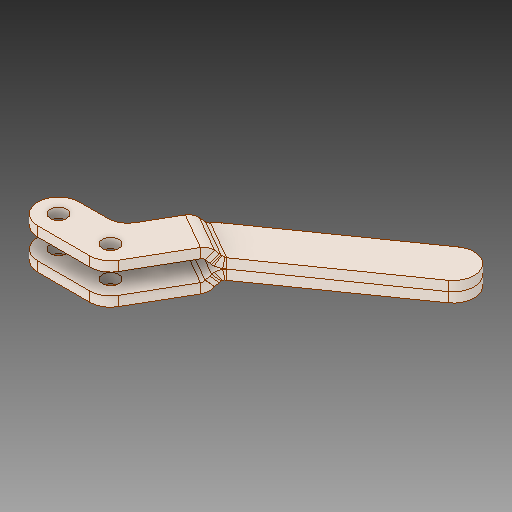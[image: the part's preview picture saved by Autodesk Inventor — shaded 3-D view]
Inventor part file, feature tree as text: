
AUTODESK INVENTOR PART (.ipt)
format: ipt  version: 2019 (Build 230136000, 136)  size: 156,672 bytes
history: mixed  units: in
note: dims shown in document units (in); Inventor stores cm internally (conversion verified against a paired STEP export)
features: other x1, mirror x1, imported_body x1
ambient origin geometry x8: Origin, YZ Plane, XZ Plane, XY Plane, X Axis, Y Axis, Z Axis, Center Point
bodies: Solid1 (imported_parasolid), Solid2 (imported_parasolid)
feature tree (3):
  other  "Jog1"
  mirror  "Mirror1"
  imported_body  NMx_Import_Brep_tag  [imported B-rep: ~40 faces, bbox_mm=[13.428688, 12.35, 10.333389]]
